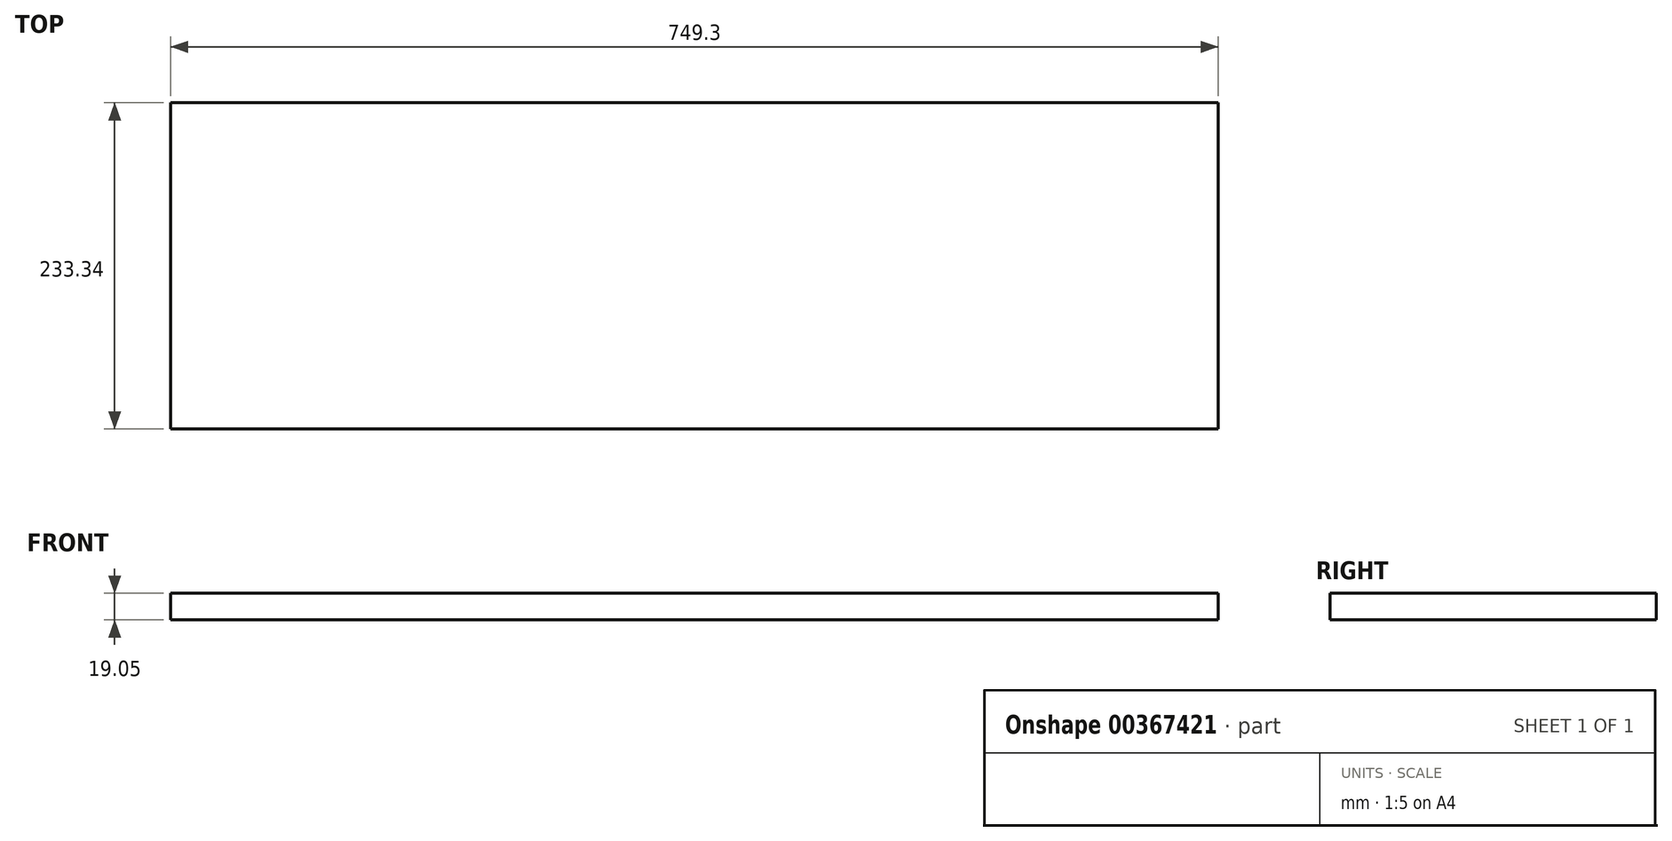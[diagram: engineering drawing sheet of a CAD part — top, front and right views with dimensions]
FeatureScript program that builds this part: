
annotation { "Feature Type Name" : "Feature", "Feature Type Description" : "" }
export const myFeature = defineFeature(function(context is Context, id is Id, definition is map)
    precondition{}
    {
        {
            var Q0;
            Q0=qCreatedBy(makeId("Top.planeOp"),FACE);
            var sketch = newSketch(context, id + "F0", { "sketchPlane" : qUnion([Q0])});
            skLineSegment(sketch, "E0.bottom", {"start": v(374.65, 116.67) * mm, "end": v(-374.65, 116.67) * mm});
            skLineSegment(sketch, "E0.top", {"start": v(374.65, -116.67) * mm, "end": v(-374.65, -116.67) * mm});
            skLineSegment(sketch, "E0.left", {"start": v(374.65, 116.67) * mm, "end": v(374.65, -116.67) * mm});
            skLineSegment(sketch, "E0.right", {"start": v(-374.65, 116.67) * mm, "end": v(-374.65, -116.67) * mm});
            skPoint(sketch, "E0.middle", {"position": v(0, 0) * mm});
            skSolve(sketch);
        }
        {
            var Q0;
            Q0 = qSketchRegion(id + "F0", true);
            extrude(context, id + "F1", {"entities" : qUnion([Q0]), "depth" : 19.05 * mm});
        }
    });
